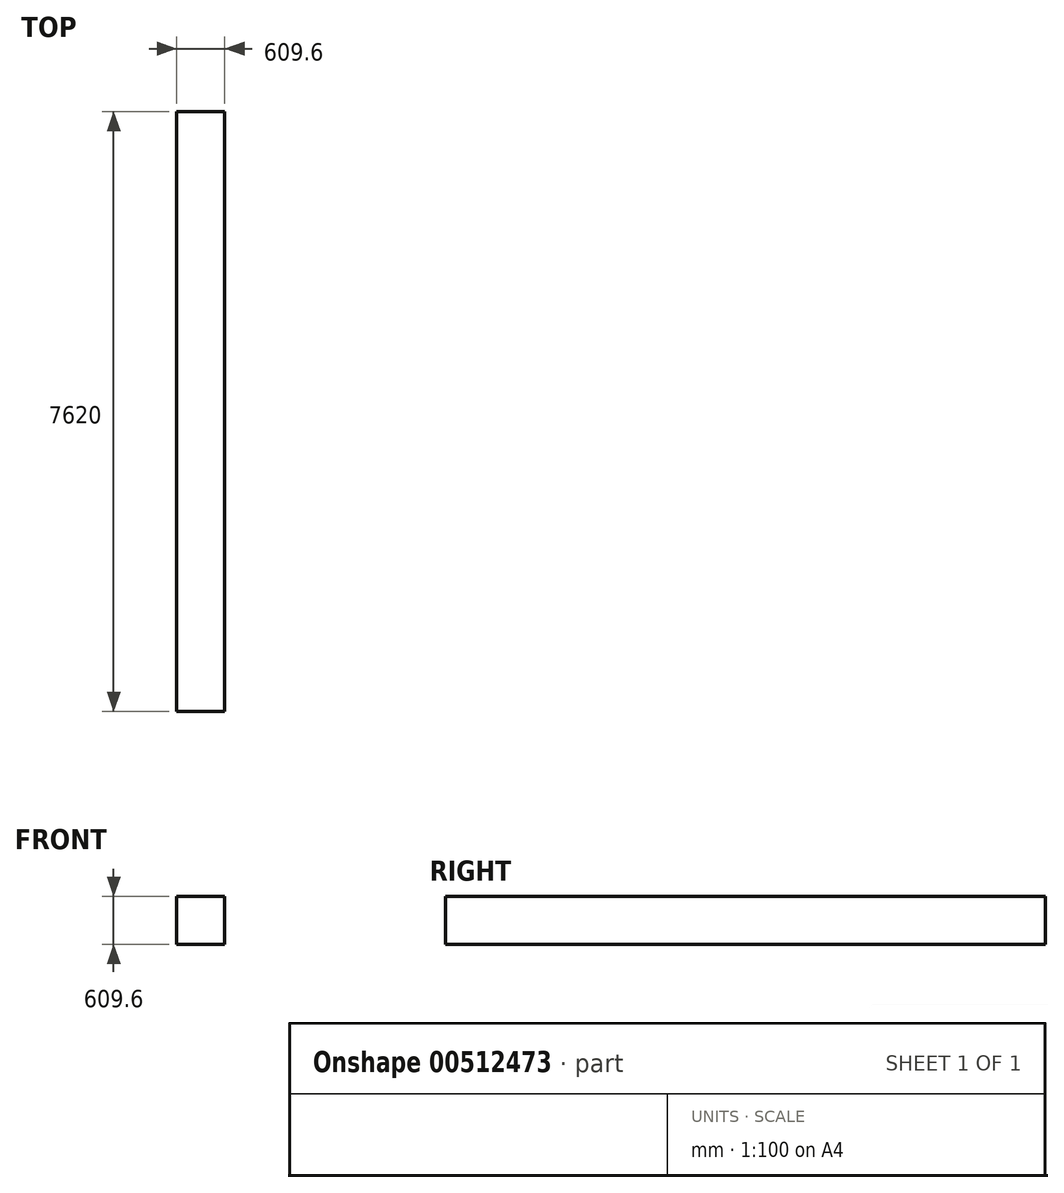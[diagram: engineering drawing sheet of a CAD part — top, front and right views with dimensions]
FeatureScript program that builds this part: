
annotation { "Feature Type Name" : "Feature", "Feature Type Description" : "" }
export const myFeature = defineFeature(function(context is Context, id is Id, definition is map)
    precondition{}
    {
        {
            var Q0;
            Q0=qCreatedBy(makeId("Top.planeOp"),FACE);
            var sketch = newSketch(context, id + "F0", { "sketchPlane" : qUnion([Q0])});
            skLineSegment(sketch, "E0.bottom", {"start": v(0, 7620) * mm, "end": v(609.6, 7620) * mm});
            skLineSegment(sketch, "E0.top", {"start": v(0, 0) * mm, "end": v(609.6, 0) * mm});
            skLineSegment(sketch, "E0.left", {"start": v(0, 7620) * mm, "end": v(0, 0) * mm});
            skLineSegment(sketch, "E0.right", {"start": v(609.6, 7620) * mm, "end": v(609.6, 0) * mm});
            skSolve(sketch);
        }
        {
            var Q0;
            Q0=qSketchRegion(id+"F0",true);
            extrude(context, id + "F1", {"entities" : qUnion([Q0]), "depth" : 609.6 * mm});
        }
    });
